# Revit family: Thorn FEROZ
name_source: partatom
category: Lighting Fixtures
revit_build: Autodesk Revit 2016 (Build: 20150220_1215(x64)
units: mm (PartAtom-declared; Revit-internal decimal feet)

## family parameters
Cut with Voids When Loaded = No
Host = Face
Light Source = Yes
OmniClass Number = 23.80.70.11
OmniClass Title = Luminaries for Internal Lighting
Part Type = Normal
Room Calculation Point = No
Round Connector Dimension = Use Diameter
Shared = No

## types (6) — shared parameters
Assembly Code = D5020200
Body = Thorn_Metal_Grey
Color Filter = 16777215
Cover = Thorn_PMMA
Description = LED waterproof luminaire
Dimming Lamp Color Temperature Shift = <None>
Emit Shape Visible in Rendering = No
Emit from Rectangle Length = 167 mm  [stored 0.5479 ft]
Height = 90 mm  [stored 0.295276 ft]
Lamp = LED
Manufacturer = Thorn Lighting
Tilt Angle = -90.00°
Voltage = 230 V
Width = 167 mm  [stored 0.5479 ft]
zero-valued in all types: Default Elevation

## per-type parameters (varying)
| type | Apparent Load | Emit from Rectangle Width | Length | Model | Photometric Web File | URL |
| FEROZ LED10000 CL L1500 | 82 VA | 1444 mm  [stored 4.73753 ft] | 1544 mm  [stored 5.06562 ft] | 96630864 | 96630864_(STD).IES | www.thornlighting.com/96630864 |
| FEROZ LED2500 CL L600 | 19 VA | 580 mm | 680 mm | 96630862 | 96630862_(STD).IES | www.thornlighting.com/96630862 |
| FEROZ LED5400 CL L1200 | 39 VA | 1156 mm | 1256 mm | 96630863 | 96630863_(STD).IES | www.thornlighting.com/96630863 |
| FEROZ LED2000 OP L600 | 19 VA | 580 mm | 680 mm | 96630867 | 96630867_(STD).IES | www.thornlighting.com/96630867 |
| FEROZ LED4200 OP L1200 | 39 VA | 1156 mm | 1256 mm | 96630868 | 96630868_(STD).IES | www.thornlighting.com/96630868 |
| FEROZ LED8000 OP L1500 | 82 VA | 1444 mm  [stored 4.73753 ft] | 1544 mm  [stored 5.06562 ft] | 96630869 | 96630869_(STD).IES | www.thornlighting.com/96630869 |

note: [stored X ft] marks values corroborated as IEEE doubles in the binary element streams (Revit-internal decimal feet)

## geometry (parser evidence)
native form markers: Sweep x7
no freeform markers — native parametric forms only
